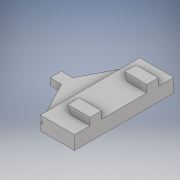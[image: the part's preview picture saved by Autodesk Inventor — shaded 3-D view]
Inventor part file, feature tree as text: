
AUTODESK INVENTOR PART (.ipt)
format: ipt  version: 2017 (Build 210142000, 142)  size: 144,896 bytes
history: native  units: mm
features: extrude x3, sketch x3, draft x2, other x1
ambient origin geometry x8: Origin, YZ Plane, XZ Plane, XY Plane, X Axis, Y Axis, Z Axis, Center Point
bodies: Solid1 (feature_tree)
feature tree (9):
  extrude  "Gancho"  Depth=43.6mm
  extrude  "Deslizador"  Depth=3.0mm TaperAngle=0.0deg
  other  "Agarre Deslizador"
  extrude  "Diente"  [1 undecoded]
  draft  "FaceDraft4"
  draft  "FaceDraft5"
  sketch  "Sketch1"  dims[d0=15.0mm d1=43.6mm]
  sketch  "Sketch2"  dims[d2=5.0mm d4=3.0mm d5=0.0mm]
  sketch  "Sketch3"  dims[d6=3.0mm d7=0.0mm d8=-3.490659mm d15=10.0mm d17=5.0mm d18=9.8mm d19=20.0mm d20=3.2mm d21=0.0mm d22=-3.490659mm d23=-3.490659mm]
note: 1 required parameter value undecoded (feature->parameter linkage not recoverable at this tier; creation-order binding heuristic only, values carry confidence <= 0.55)
